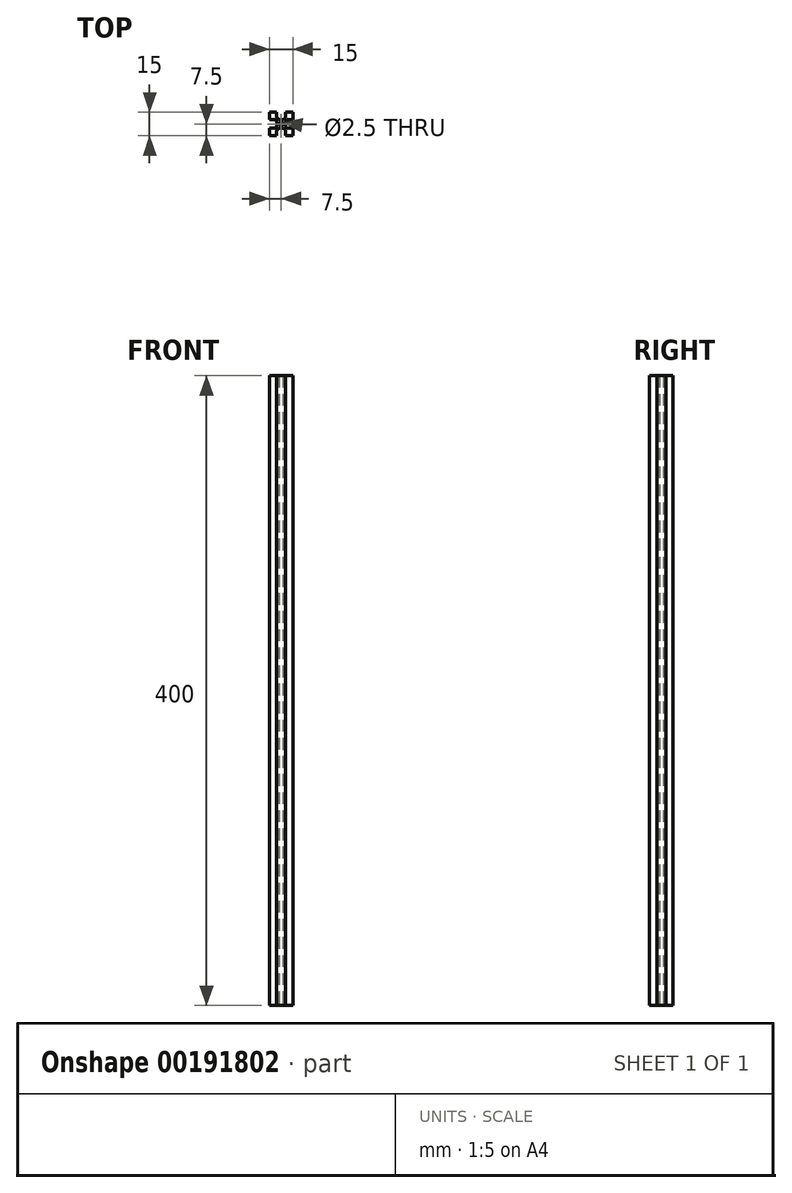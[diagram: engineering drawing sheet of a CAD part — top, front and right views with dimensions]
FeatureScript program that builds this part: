
annotation { "Feature Type Name" : "Feature", "Feature Type Description" : "" }
export const myFeature = defineFeature(function(context is Context, id is Id, definition is map)
    precondition{}
    {
        {
            var Q0;
            Q0=qCreatedBy(makeId("Top.planeOp"),FACE);
            var sketch = newSketch(context, id + "F0", { "sketchPlane" : qUnion([Q0])});
            skLineSegment(sketch, "E0.bottom", {"start": v(-7.5, 7.5) * mm, "end": v(7.5, 7.5) * mm});
            skLineSegment(sketch, "E0.top", {"start": v(-7.5, -7.5) * mm, "end": v(7.5, -7.5) * mm});
            skLineSegment(sketch, "E0.left", {"start": v(-7.5, 7.5) * mm, "end": v(-7.5, -7.5) * mm});
            skLineSegment(sketch, "E0.right", {"start": v(7.5, 7.5) * mm, "end": v(7.5, -7.5) * mm});
            skPoint(sketch, "E0.middle", {"position": v(0, 0) * mm});
            skLineSegment(sketch, "E1.bottom", {"start": v(-2.85, -7.5) * mm, "end": v(2.85, -7.5) * mm});
            skLineSegment(sketch, "E1.top", {"start": v(-0.85, -2.8) * mm, "end": v(0.85, -2.8) * mm});
            skLineSegment(sketch, "E1.left", {"start": v(-2.85, -7.5) * mm, "end": v(-2.85, -4.8) * mm});
            skLineSegment(sketch, "E1.right", {"start": v(2.85, -7.5) * mm, "end": v(2.85, -4.8) * mm});
            skLineSegment(sketch, "E2.bottom", {"start": v(7.5, -2.85) * mm, "end": v(4.8, -2.85) * mm});
            skLineSegment(sketch, "E2.top", {"start": v(7.5, 2.85) * mm, "end": v(4.8, 2.85) * mm});
            skLineSegment(sketch, "E2.left", {"start": v(7.5, -2.85) * mm, "end": v(7.5, 2.85) * mm});
            skLineSegment(sketch, "E2.right", {"start": v(2.8, -0.85) * mm, "end": v(2.8, 0.85) * mm});
            skLineSegment(sketch, "E3.bottom", {"start": v(2.85, 7.5) * mm, "end": v(-2.85, 7.5) * mm});
            skLineSegment(sketch, "E3.top", {"start": v(0.85, 2.8) * mm, "end": v(-0.85, 2.8) * mm});
            skLineSegment(sketch, "E3.left", {"start": v(2.85, 7.5) * mm, "end": v(2.85, 4.8) * mm});
            skLineSegment(sketch, "E3.right", {"start": v(-2.85, 7.5) * mm, "end": v(-2.85, 4.8) * mm});
            skLineSegment(sketch, "E4.bottom", {"start": v(-7.5, 2.85) * mm, "end": v(-4.8, 2.85) * mm});
            skLineSegment(sketch, "E4.top", {"start": v(-7.5, -2.85) * mm, "end": v(-4.8, -2.85) * mm});
            skLineSegment(sketch, "E4.left", {"start": v(-7.5, 2.85) * mm, "end": v(-7.5, -2.85) * mm});
            skLineSegment(sketch, "E4.right", {"start": v(-2.8, 0.85) * mm, "end": v(-2.8, -0.85) * mm});
            skCircle(sketch, "E5", {"center": v(0, 0) * mm, "radius": 1.25 * mm});
            skPoint(sketch, "E6.visualSharp", {"position": v(-2.85, -2.8) * mm});
            skArc(sketch, "E6.filletArc", {"start": v(-0.85, -2.8) * mm, "mid": v(-2.26, -3.39) * mm, "end": v(-2.85, -4.8) * mm});
            skPoint(sketch, "E7.visualSharp", {"position": v(2.85, -2.8) * mm});
            skArc(sketch, "E7.filletArc", {"start": v(2.85, -4.8) * mm, "mid": v(2.26, -3.39) * mm, "end": v(0.85, -2.8) * mm});
            skPoint(sketch, "E8.visualSharp", {"position": v(2.8, -2.85) * mm});
            skArc(sketch, "E8.filletArc", {"start": v(2.8, -0.85) * mm, "mid": v(3.39, -2.26) * mm, "end": v(4.8, -2.85) * mm});
            skPoint(sketch, "E9.visualSharp", {"position": v(2.8, 2.85) * mm});
            skArc(sketch, "E9.filletArc", {"start": v(4.8, 2.85) * mm, "mid": v(3.39, 2.26) * mm, "end": v(2.8, 0.85) * mm});
            skPoint(sketch, "E10.visualSharp", {"position": v(2.85, 2.8) * mm});
            skArc(sketch, "E10.filletArc", {"start": v(0.85, 2.8) * mm, "mid": v(2.26, 3.39) * mm, "end": v(2.85, 4.8) * mm});
            skPoint(sketch, "E11.visualSharp", {"position": v(-2.85, 2.8) * mm});
            skArc(sketch, "E11.filletArc", {"start": v(-2.85, 4.8) * mm, "mid": v(-2.26, 3.39) * mm, "end": v(-0.85, 2.8) * mm});
            skPoint(sketch, "E12.visualSharp", {"position": v(-2.8, 2.85) * mm});
            skArc(sketch, "E12.filletArc", {"start": v(-2.8, 0.85) * mm, "mid": v(-3.39, 2.26) * mm, "end": v(-4.8, 2.85) * mm});
            skPoint(sketch, "E13.visualSharp", {"position": v(-2.8, -2.85) * mm});
            skArc(sketch, "E13.filletArc", {"start": v(-4.8, -2.85) * mm, "mid": v(-3.39, -2.26) * mm, "end": v(-2.8, -0.85) * mm});
            skLineSegment(sketch, "E14.bottom", {"start": v(-2.85, -7.5) * mm, "end": v(-1.7, -7.5) * mm});
            skLineSegment(sketch, "E14.top", {"start": v(-2.85, -6.4) * mm, "end": v(-1.7, -6.4) * mm});
            skLineSegment(sketch, "E14.left", {"start": v(-2.85, -7.5) * mm, "end": v(-2.85, -6.4) * mm});
            skLineSegment(sketch, "E14.right", {"start": v(-1.7, -7.5) * mm, "end": v(-1.7, -6.4) * mm});
            skLineSegment(sketch, "E15.bottom", {"start": v(2.85, -7.5) * mm, "end": v(1.7, -7.5) * mm});
            skLineSegment(sketch, "E15.top", {"start": v(2.85, -6.4) * mm, "end": v(1.7, -6.4) * mm});
            skLineSegment(sketch, "E15.left", {"start": v(2.85, -7.5) * mm, "end": v(2.85, -6.4) * mm});
            skLineSegment(sketch, "E15.right", {"start": v(1.7, -7.5) * mm, "end": v(1.7, -6.4) * mm});
            skLineSegment(sketch, "E16.bottom", {"start": v(7.5, -2.85) * mm, "end": v(6.4, -2.85) * mm});
            skLineSegment(sketch, "E16.top", {"start": v(7.5, -1.7) * mm, "end": v(6.4, -1.7) * mm});
            skLineSegment(sketch, "E16.left", {"start": v(7.5, -2.85) * mm, "end": v(7.5, -1.7) * mm});
            skLineSegment(sketch, "E16.right", {"start": v(6.4, -2.85) * mm, "end": v(6.4, -1.7) * mm});
            skLineSegment(sketch, "E17.bottom", {"start": v(7.5, 2.85) * mm, "end": v(6.4, 2.85) * mm});
            skLineSegment(sketch, "E17.top", {"start": v(7.5, 1.7) * mm, "end": v(6.4, 1.7) * mm});
            skLineSegment(sketch, "E17.left", {"start": v(7.5, 2.85) * mm, "end": v(7.5, 1.7) * mm});
            skLineSegment(sketch, "E17.right", {"start": v(6.4, 2.85) * mm, "end": v(6.4, 1.7) * mm});
            skLineSegment(sketch, "E18.bottom", {"start": v(2.85, 7.5) * mm, "end": v(1.7, 7.5) * mm});
            skLineSegment(sketch, "E18.top", {"start": v(2.85, 6.4) * mm, "end": v(1.7, 6.4) * mm});
            skLineSegment(sketch, "E18.left", {"start": v(2.85, 7.5) * mm, "end": v(2.85, 6.4) * mm});
            skLineSegment(sketch, "E18.right", {"start": v(1.7, 7.5) * mm, "end": v(1.7, 6.4) * mm});
            skLineSegment(sketch, "E19.bottom", {"start": v(-2.85, 7.5) * mm, "end": v(-1.7, 7.5) * mm});
            skLineSegment(sketch, "E19.top", {"start": v(-2.85, 6.4) * mm, "end": v(-1.7, 6.4) * mm});
            skLineSegment(sketch, "E19.left", {"start": v(-2.85, 7.5) * mm, "end": v(-2.85, 6.4) * mm});
            skLineSegment(sketch, "E19.right", {"start": v(-1.7, 7.5) * mm, "end": v(-1.7, 6.4) * mm});
            skLineSegment(sketch, "E20.bottom", {"start": v(-7.5, 2.85) * mm, "end": v(-6.4, 2.85) * mm});
            skLineSegment(sketch, "E20.top", {"start": v(-7.5, 1.7) * mm, "end": v(-6.4, 1.7) * mm});
            skLineSegment(sketch, "E20.left", {"start": v(-7.5, 2.85) * mm, "end": v(-7.5, 1.7) * mm});
            skLineSegment(sketch, "E20.right", {"start": v(-6.4, 2.85) * mm, "end": v(-6.4, 1.7) * mm});
            skLineSegment(sketch, "E21.bottom", {"start": v(-7.5, -2.85) * mm, "end": v(-6.4, -2.85) * mm});
            skLineSegment(sketch, "E21.top", {"start": v(-7.5, -1.7) * mm, "end": v(-6.4, -1.7) * mm});
            skLineSegment(sketch, "E21.left", {"start": v(-7.5, -2.85) * mm, "end": v(-7.5, -1.7) * mm});
            skLineSegment(sketch, "E21.right", {"start": v(-6.4, -2.85) * mm, "end": v(-6.4, -1.7) * mm});
            skSolve(sketch);
        }
        {
            var Q0;
            Q0=makeQuery(id+"F0.imprint","IMPRINT",FACE,{"disambiguationData":[TD([[makeQuery(id+"F0.imprint","IMPRINT",EDGE,{"derivedFrom":sQuery(id+"F0.wireOp",EDGE,"E1.top")}),1.0]])]});
            var Q1;
            Q1=makeQuery(id+"F0.imprint","IMPRINT",FACE,{"disambiguationData":[TD([[makeQuery(id+"F0.imprint","IMPRINT",EDGE,{"derivedFrom":sQuery(id+"F0.wireOp",EDGE,"E20.bottom")}),-1.0]])]});
            var Q2;
            Q2=makeQuery(id+"F0.imprint","IMPRINT",FACE,{"disambiguationData":[TD([[makeQuery(id+"F0.imprint","IMPRINT",EDGE,{"derivedFrom":sQuery(id+"F0.wireOp",EDGE,"E21.bottom")}),1.0]])]});
            var Q3;
            Q3=makeQuery(id+"F0.imprint","IMPRINT",FACE,{"disambiguationData":[TD([[makeQuery(id+"F0.imprint","IMPRINT",EDGE,{"derivedFrom":sQuery(id+"F0.wireOp",EDGE,"E19.bottom")}),-1.0]])]});
            var Q4;
            Q4=makeQuery(id+"F0.imprint","IMPRINT",FACE,{"disambiguationData":[TD([[makeQuery(id+"F0.imprint","IMPRINT",EDGE,{"derivedFrom":sQuery(id+"F0.wireOp",EDGE,"E18.bottom")}),1.0]])]});
            var Q5;
            Q5=makeQuery(id+"F0.imprint","IMPRINT",FACE,{"disambiguationData":[TD([[makeQuery(id+"F0.imprint","IMPRINT",EDGE,{"derivedFrom":sQuery(id+"F0.wireOp",EDGE,"E17.bottom")}),1.0]])]});
            var Q6;
            Q6=makeQuery(id+"F0.imprint","IMPRINT",FACE,{"disambiguationData":[TD([[makeQuery(id+"F0.imprint","IMPRINT",EDGE,{"derivedFrom":sQuery(id+"F0.wireOp",EDGE,"E16.bottom")}),-1.0]])]});
            var Q7;
            Q7=makeQuery(id+"F0.imprint","IMPRINT",FACE,{"disambiguationData":[TD([[makeQuery(id+"F0.imprint","IMPRINT",EDGE,{"derivedFrom":sQuery(id+"F0.wireOp",EDGE,"E14.bottom")}),1.0]])]});
            var Q8;
            Q8=makeQuery(id+"F0.imprint","IMPRINT",FACE,{"disambiguationData":[TD([[makeQuery(id+"F0.imprint","IMPRINT",EDGE,{"derivedFrom":sQuery(id+"F0.wireOp",EDGE,"E15.bottom")}),-1.0]])]});
            extrude(context, id + "F1", {"entities" : qUnion([Q0, Q1, Q2, Q3, Q4, Q5, Q6, Q7, Q8]), "depth" : 400 * mm});
        }
    });
